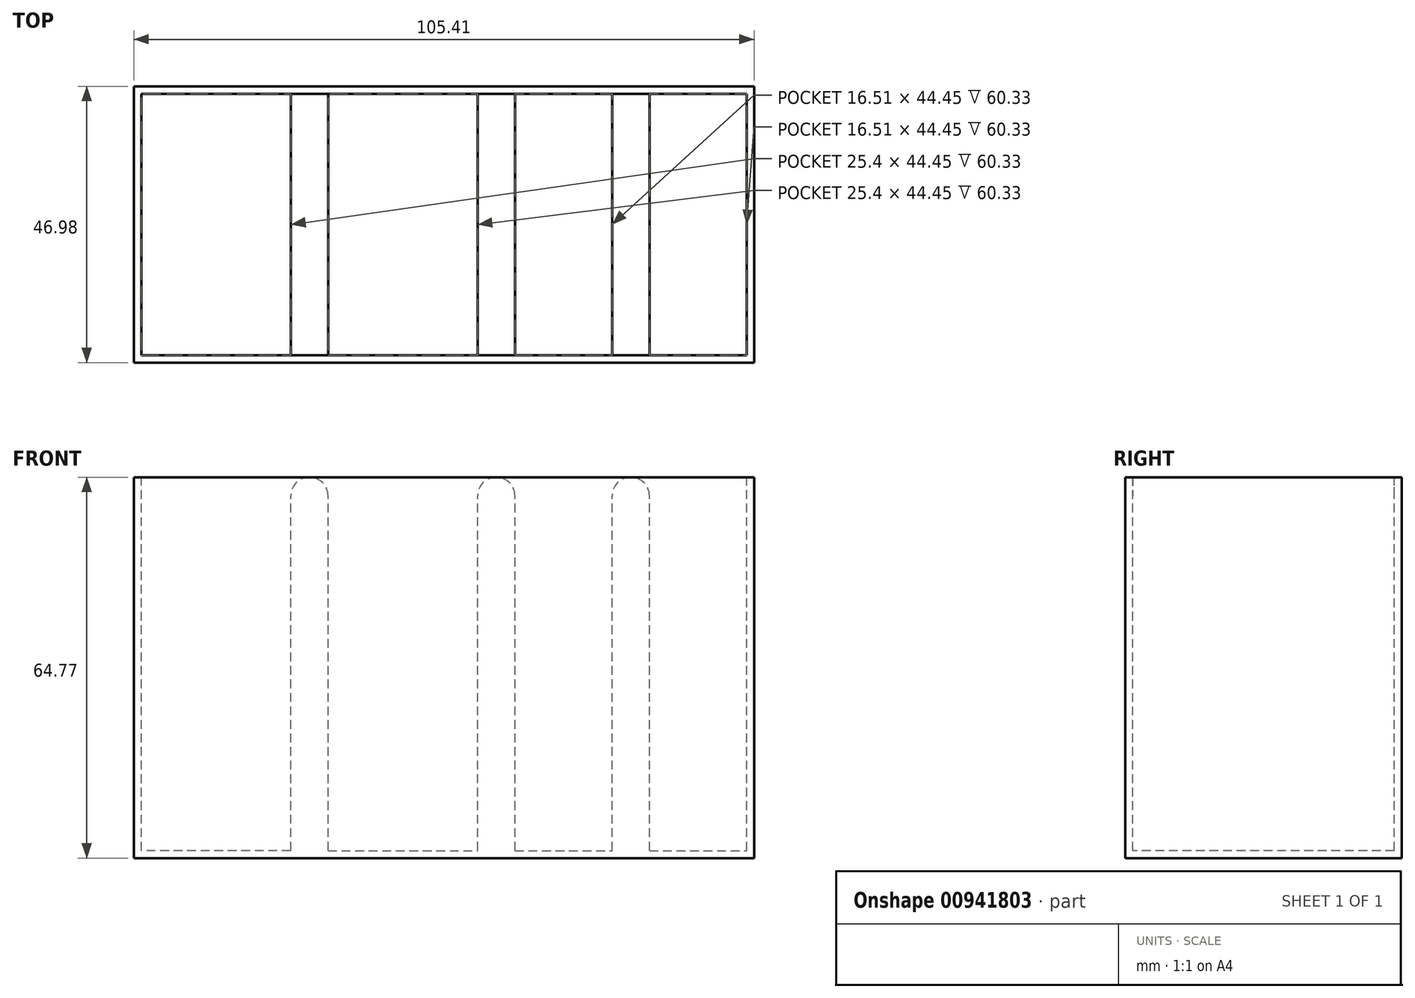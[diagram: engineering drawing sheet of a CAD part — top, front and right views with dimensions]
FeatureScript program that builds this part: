
annotation { "Feature Type Name" : "Feature", "Feature Type Description" : "" }
export const myFeature = defineFeature(function(context is Context, id is Id, definition is map)
    precondition{}
    {
        {
            var Q0;
            Q0=qCreatedBy(makeId("Top.planeOp"),FACE);
            var sketch = newSketch(context, id + "F0", { "sketchPlane" : qUnion([Q0])});
            skLineSegment(sketch, "E0.bottom", {"start": v(12.7, -22.23) * mm, "end": v(-12.7, -22.23) * mm});
            skLineSegment(sketch, "E0.top", {"start": v(12.7, 22.23) * mm, "end": v(-12.7, 22.23) * mm});
            skLineSegment(sketch, "E0.left", {"start": v(12.7, -22.23) * mm, "end": v(12.7, 22.22) * mm});
            skLineSegment(sketch, "E0.right", {"start": v(-12.7, -22.23) * mm, "end": v(-12.7, 22.22) * mm});
            skPoint(sketch, "E0.middle", {"position": v(0, 0) * mm});
            skLineSegment(sketch, "E1.bottom", {"start": v(12.7, 22.23) * mm, "end": v(19.05, 22.23) * mm});
            skLineSegment(sketch, "E1.top", {"start": v(12.7, -22.23) * mm, "end": v(19.05, -22.23) * mm});
            skLineSegment(sketch, "E1.left", {"start": v(12.7, 22.23) * mm, "end": v(12.7, -22.23) * mm});
            skLineSegment(sketch, "E1.right", {"start": v(19.05, 22.22) * mm, "end": v(19.05, -22.23) * mm});
            skLineSegment(sketch, "E2.bottom", {"start": v(19.05, 22.23) * mm, "end": v(44.45, 22.23) * mm});
            skLineSegment(sketch, "E2.top", {"start": v(19.05, -22.23) * mm, "end": v(44.45, -22.23) * mm});
            skLineSegment(sketch, "E2.left", {"start": v(19.05, 22.23) * mm, "end": v(19.05, -22.23) * mm});
            skLineSegment(sketch, "E2.right", {"start": v(44.45, 22.22) * mm, "end": v(44.45, -22.23) * mm});
            skLineSegment(sketch, "E3.bottom", {"start": v(44.45, 22.23) * mm, "end": v(50.8, 22.23) * mm});
            skLineSegment(sketch, "E3.top", {"start": v(44.45, -22.23) * mm, "end": v(50.8, -22.23) * mm});
            skLineSegment(sketch, "E3.left", {"start": v(44.45, 22.23) * mm, "end": v(44.45, -22.23) * mm});
            skLineSegment(sketch, "E3.right", {"start": v(50.8, 22.22) * mm, "end": v(50.8, -22.23) * mm});
            skLineSegment(sketch, "E4.bottom", {"start": v(50.8, 22.23) * mm, "end": v(67.31, 22.23) * mm});
            skLineSegment(sketch, "E4.top", {"start": v(50.8, -22.23) * mm, "end": v(67.31, -22.23) * mm});
            skLineSegment(sketch, "E4.left", {"start": v(50.8, 22.23) * mm, "end": v(50.8, -22.23) * mm});
            skLineSegment(sketch, "E4.right", {"start": v(67.31, 22.22) * mm, "end": v(67.31, -22.23) * mm});
            skLineSegment(sketch, "E5.bottom", {"start": v(67.31, 22.23) * mm, "end": v(73.66, 22.23) * mm});
            skLineSegment(sketch, "E5.top", {"start": v(67.31, -22.23) * mm, "end": v(73.66, -22.23) * mm});
            skLineSegment(sketch, "E5.left", {"start": v(67.31, 22.23) * mm, "end": v(67.31, -22.23) * mm});
            skLineSegment(sketch, "E5.right", {"start": v(73.66, 22.22) * mm, "end": v(73.66, -22.23) * mm});
            skLineSegment(sketch, "E6.left", {"start": v(73.66, 22.23) * mm, "end": v(73.66, 0) * mm});
            skLineSegment(sketch, "E7.bottom", {"start": v(73.66, 22.23) * mm, "end": v(90.17, 22.23) * mm});
            skLineSegment(sketch, "E7.top", {"start": v(73.66, -22.23) * mm, "end": v(90.17, -22.23) * mm});
            skLineSegment(sketch, "E7.left", {"start": v(73.66, 22.23) * mm, "end": v(73.66, -22.23) * mm});
            skLineSegment(sketch, "E7.right", {"start": v(90.17, 22.23) * mm, "end": v(90.17, -22.23) * mm});
            skLineSegment(sketch, "E8", {"start": v(90.17, 22.23) * mm, "end": v(91.44, 22.23) * mm});
            skLineSegment(sketch, "E9.bottom", {"start": v(90.17, -22.23) * mm, "end": v(91.44, -22.23) * mm});
            skLineSegment(sketch, "E9.left", {"start": v(90.17, -22.23) * mm, "end": v(90.17, 22.23) * mm});
            skLineSegment(sketch, "E9.right", {"start": v(91.44, -22.23) * mm, "end": v(91.44, 22.22) * mm});
            skLineSegment(sketch, "E10.bottom", {"start": v(-12.7, -22.23) * mm, "end": v(91.44, -22.23) * mm});
            skLineSegment(sketch, "E10.top", {"start": v(-12.7, -22.23) * mm, "end": v(91.44, -22.23) * mm});
            skLineSegment(sketch, "E10.left", {"start": v(-12.7, -22.23) * mm, "end": v(-12.7, -22.23) * mm});
            skLineSegment(sketch, "E10.right", {"start": v(91.44, -22.22) * mm, "end": v(91.44, -22.23) * mm});
            skLineSegment(sketch, "E11.bottom", {"start": v(-12.7, 22.23) * mm, "end": v(-13.97, 22.23) * mm});
            skLineSegment(sketch, "E11.left", {"start": v(-12.7, 22.23) * mm, "end": v(-12.7, -22.23) * mm});
            skLineSegment(sketch, "E11.right", {"start": v(-13.97, 22.22) * mm, "end": v(-13.97, -22.23) * mm});
            skLineSegment(sketch, "E12", {"start": v(91.44, -22.23) * mm, "end": v(91.44, -23.5) * mm});
            skLineSegment(sketch, "E13.top", {"start": v(-13.97, -23.5) * mm, "end": v(91.44, -23.5) * mm});
            skLineSegment(sketch, "E13.left", {"start": v(-13.97, -22.23) * mm, "end": v(-13.97, -23.5) * mm});
            skLineSegment(sketch, "E14", {"start": v(-13.97, 22.23) * mm, "end": v(-13.97, 23.5) * mm});
            skLineSegment(sketch, "E15.bottom", {"start": v(91.44, 22.23) * mm, "end": v(-13.97, 22.23) * mm});
            skLineSegment(sketch, "E15.top", {"start": v(91.44, 23.5) * mm, "end": v(-13.97, 23.5) * mm});
            skLineSegment(sketch, "E15.left", {"start": v(91.44, 22.23) * mm, "end": v(91.44, 23.5) * mm});
            skSolve(sketch);
        }
        {
            var Q0;
            Q0=makeQuery(id+"F0.imprint","IMPRINT",FACE,{"disambiguationData":[TD([[makeQuery(id+"F0.imprint","IMPRINT",EDGE,{"derivedFrom":sQuery(id+"F0.wireOp",EDGE,"E0.bottom")}),1.0]])]});
            var Q1;
            Q1=makeQuery(id+"F0.imprint","IMPRINT",FACE,{"disambiguationData":[TD([[makeQuery(id+"F0.imprint","IMPRINT",EDGE,{"derivedFrom":sQuery(id+"F0.wireOp",EDGE,"E0.top")}),-1.0]])]});
            var Q2;
            Q2=makeQuery(id+"F0.imprint","IMPRINT",FACE,{"disambiguationData":[TD([[makeQuery(id+"F0.imprint","IMPRINT",EDGE,{"derivedFrom":sQuery(id+"F0.wireOp",EDGE,"E7.right")}),1.0]])]});
            var Q3;
            Q3=makeQuery(id+"F0.imprint","IMPRINT",FACE,{"disambiguationData":[TD([[makeQuery(id+"F0.imprint","IMPRINT",EDGE,{"derivedFrom":sQuery(id+"F0.wireOp",EDGE,"E4.right")}),1.0]])]});
            var Q4;
            Q4=makeQuery(id+"F0.imprint","IMPRINT",FACE,{"disambiguationData":[TD([[makeQuery(id+"F0.imprint","IMPRINT",EDGE,{"derivedFrom":sQuery(id+"F0.wireOp",EDGE,"E2.right")}),1.0]])]});
            var Q5;
            Q5=makeQuery(id+"F0.imprint","IMPRINT",FACE,{"disambiguationData":[TD([[makeQuery(id+"F0.imprint","IMPRINT",EDGE,{"derivedFrom":sQuery(id+"F0.wireOp",EDGE,"E0.left")}),-1.0]])]});
            extrude(context, id + "F1", {"entities" : qUnion([Q0, Q1, Q2, Q3, Q4, Q5]), "oppositeDirection" : true, "depth" : 63.5 * mm, "offsetDistance" : 25 * mm});
        }
        {
            var Q0;
            Q0=makeQuery(id+"F1.opExtrude","CAP_FACE",FACE,{"disambiguationData":[OSD([sQuery(id+"F0.wireOp",EDGE,"E0.bottom"),sQuery(id+"F0.wireOp",EDGE,"E0.top"),sQuery(id+"F0.wireOp",EDGE,"E0.left"),sQuery(id+"F0.wireOp",EDGE,"E0.right"),sQuery(id+"F0.wireOp",EDGE,"E1.right"),sQuery(id+"F0.wireOp",EDGE,"E2.bottom"),sQuery(id+"F0.wireOp",EDGE,"E2.top"),sQuery(id+"F0.wireOp",EDGE,"E2.right"),sQuery(id+"F0.wireOp",EDGE,"E3.right"),sQuery(id+"F0.wireOp",EDGE,"E4.bottom"),sQuery(id+"F0.wireOp",EDGE,"E4.top"),sQuery(id+"F0.wireOp",EDGE,"E4.right"),sQuery(id+"F0.wireOp",EDGE,"E5.right"),sQuery(id+"F0.wireOp",EDGE,"E7.bottom"),sQuery(id+"F0.wireOp",EDGE,"E7.top"),sQuery(id+"F0.wireOp",EDGE,"E7.right"),sQuery(id+"F0.wireOp",EDGE,"E9.right"),sQuery(id+"F0.wireOp",EDGE,"E11.right"),sQuery(id+"F0.wireOp",EDGE,"E12"),sQuery(id+"F0.wireOp",EDGE,"E13.top"),sQuery(id+"F0.wireOp",EDGE,"E13.left"),sQuery(id+"F0.wireOp",EDGE,"E14"),sQuery(id+"F0.wireOp",EDGE,"E15.top"),sQuery(id+"F0.wireOp",EDGE,"E15.left")])],"isStart":false});
            var sketch = newSketch(context, id + "F2", { "sketchPlane" : qUnion([Q0])});
            skLineSegment(sketch, "E16.bottom", {"start": v(-13.97, 23.5) * mm, "end": v(91.44, 23.5) * mm});
            skLineSegment(sketch, "E16.top", {"start": v(-13.97, -23.5) * mm, "end": v(91.44, -23.5) * mm});
            skLineSegment(sketch, "E16.left", {"start": v(-13.97, 23.5) * mm, "end": v(-13.97, -23.5) * mm});
            skLineSegment(sketch, "E16.right", {"start": v(91.44, 23.5) * mm, "end": v(91.44, -23.5) * mm});
            skSolve(sketch);
        }
        {
            var Q0;
            Q0 = qSketchRegion(id + "F2", true);
            extrude(context, id + "F3", {"entities" : qUnion([Q0]), "operationType" : NewBodyOperationType.ADD, "depth" : 1.27 * mm, "offsetDistance" : 25 * mm});
        }
        {
            var Q0;
            Q0=makeQuery(id+"F1.opExtrude","CAP_EDGE",EDGE,{"disambiguationData":[OSD([sQuery(id+"F0.wireOp",EDGE,"E1.right")])],"isStart":true});
            var Q1;
            Q1=makeQuery(id+"F1.opExtrude","CAP_EDGE",EDGE,{"disambiguationData":[OSD([sQuery(id+"F0.wireOp",EDGE,"E0.left")])],"isStart":true});
            var Q2;
            Q2=makeQuery(id+"F1.opExtrude","CAP_EDGE",EDGE,{"disambiguationData":[OSD([sQuery(id+"F0.wireOp",EDGE,"E2.right")])],"isStart":true});
            var Q3;
            Q3=makeQuery(id+"F1.opExtrude","CAP_EDGE",EDGE,{"disambiguationData":[OSD([sQuery(id+"F0.wireOp",EDGE,"E3.right")])],"isStart":true});
            var Q4;
            Q4=makeQuery(id+"F1.opExtrude","CAP_EDGE",EDGE,{"disambiguationData":[OSD([sQuery(id+"F0.wireOp",EDGE,"E4.right")])],"isStart":true});
            var Q5;
            Q5=makeQuery(id+"F1.opExtrude","CAP_EDGE",EDGE,{"disambiguationData":[OSD([sQuery(id+"F0.wireOp",EDGE,"E5.right")])],"isStart":true});
            fillet(context, id + "F4", {"entities" : qUnion([Q0, Q1, Q2, Q3, Q4, Q5]), "radius" : 3.17 * mm, "tangentPropagation" : true, "allowEdgeOverflow" : false});
        }
    });
